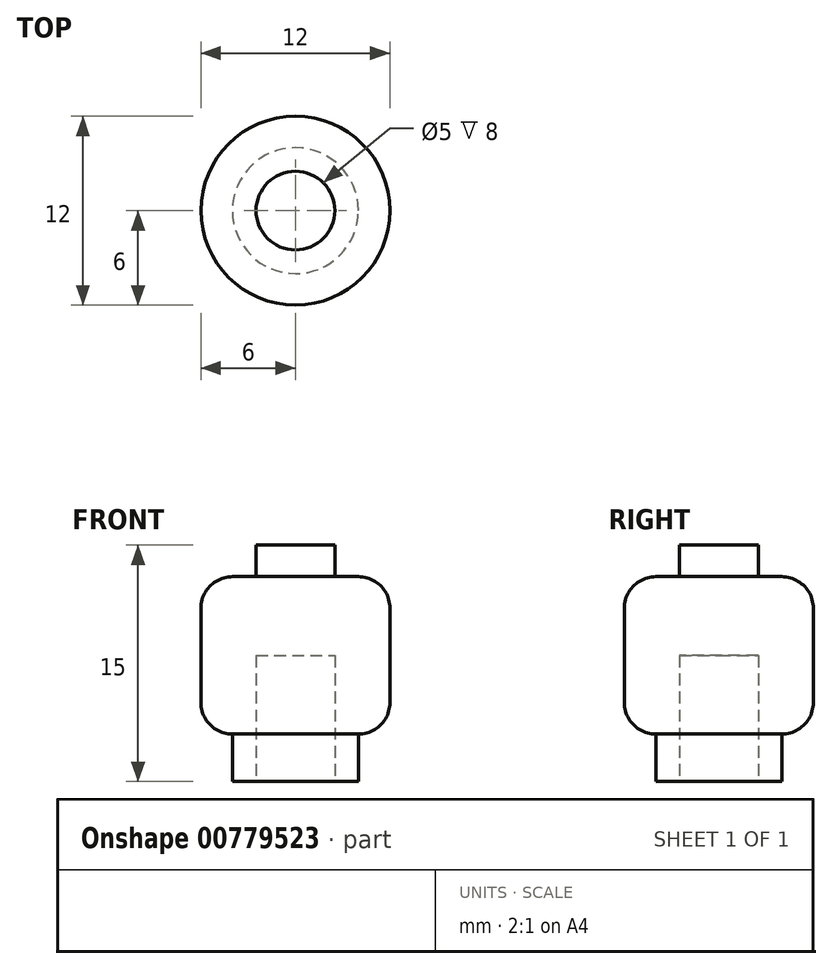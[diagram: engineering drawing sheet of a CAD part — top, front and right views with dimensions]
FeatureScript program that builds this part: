
annotation { "Feature Type Name" : "Feature", "Feature Type Description" : "" }
export const myFeature = defineFeature(function(context is Context, id is Id, definition is map)
    precondition{}
    {
        {
            var Q0;
            Q0=qCreatedBy(makeId("Top.planeOp"),FACE);
            var sketch = newSketch(context, id + "F0", { "sketchPlane" : qUnion([Q0])});
            skCircle(sketch, "E0", {"center": v(0, 0) * mm, "radius": 4 * mm});
            skSolve(sketch);
        }
        {
            var Q0;
            Q0 = qSketchRegion(id + "F0", true);
            extrude(context, id + "F1", {"entities" : qUnion([Q0]), "depth" : 3 * mm, "offsetDistance" : 25 * mm});
        }
        {
            var Q0;
            Q0=makeQuery(id+"F1.opExtrude","CAP_FACE",FACE,{"disambiguationData":[OSD([sQuery(id+"F0.wireOp",EDGE,"E0")])],"isStart":false});
            var sketch = newSketch(context, id + "F2", { "sketchPlane" : qUnion([Q0])});
            skCircle(sketch, "E1", {"center": v(0, 0) * mm, "radius": 6 * mm});
            skSolve(sketch);
        }
        {
            var Q0;
            Q0 = qSketchRegion(id + "F2", true);
            extrude(context, id + "F3", {"entities" : qUnion([Q0]), "operationType" : NewBodyOperationType.ADD, "depth" : 10 * mm, "offsetDistance" : 25 * mm});
        }
        {
            var Q0;
            Q0=makeQuery(id+"F3.opExtrude","CAP_EDGE",EDGE,{"disambiguationData":[OSD([sQuery(id+"F2.wireOp",EDGE,"E1")])],"isStart":false});
            var Q1;
            Q1=makeQuery(id+"F3.opExtrude","CAP_EDGE",EDGE,{"disambiguationData":[OSD([sQuery(id+"F2.wireOp",EDGE,"E1")])],"isStart":true});
            fillet(context, id + "F4", {"entities" : qUnion([Q0, Q1]), "radius" : 2 * mm, "tangentPropagation" : true, "allowEdgeOverflow" : false});
        }
        {
            var Q0;
            Q0=makeQuery(id+"F1.opExtrude","CAP_FACE",FACE,{"disambiguationData":[OSD([sQuery(id+"F0.wireOp",EDGE,"E0")])],"isStart":true});
            var sketch = newSketch(context, id + "F5", { "sketchPlane" : qUnion([Q0])});
            skCircle(sketch, "E2", {"center": v(0, 0) * mm, "radius": 2.5 * mm});
            skSolve(sketch);
        }
        {
            var Q0;
            Q0 = qSketchRegion(id + "F5", true);
            extrude(context, id + "F6", {"entities" : qUnion([Q0]), "operationType" : NewBodyOperationType.REMOVE, "oppositeDirection" : true, "depth" : 8 * mm, "offsetDistance" : 25 * mm});
        }
        {
            var Q0;
            Q0=makeQuery(id+"F3.opExtrude","CAP_FACE",FACE,{"disambiguationData":[OSD([sQuery(id+"F2.wireOp",EDGE,"E1")])],"isStart":false});
            var sketch = newSketch(context, id + "F7", { "sketchPlane" : qUnion([Q0])});
            skCircle(sketch, "E3", {"center": v(0, 0) * mm, "radius": 2.5 * mm});
            skSolve(sketch);
        }
        {
            var Q0;
            Q0 = qSketchRegion(id + "F7", true);
            extrude(context, id + "F8", {"entities" : qUnion([Q0]), "operationType" : NewBodyOperationType.ADD, "depth" : 2 * mm, "offsetDistance" : 25 * mm});
        }
    });
